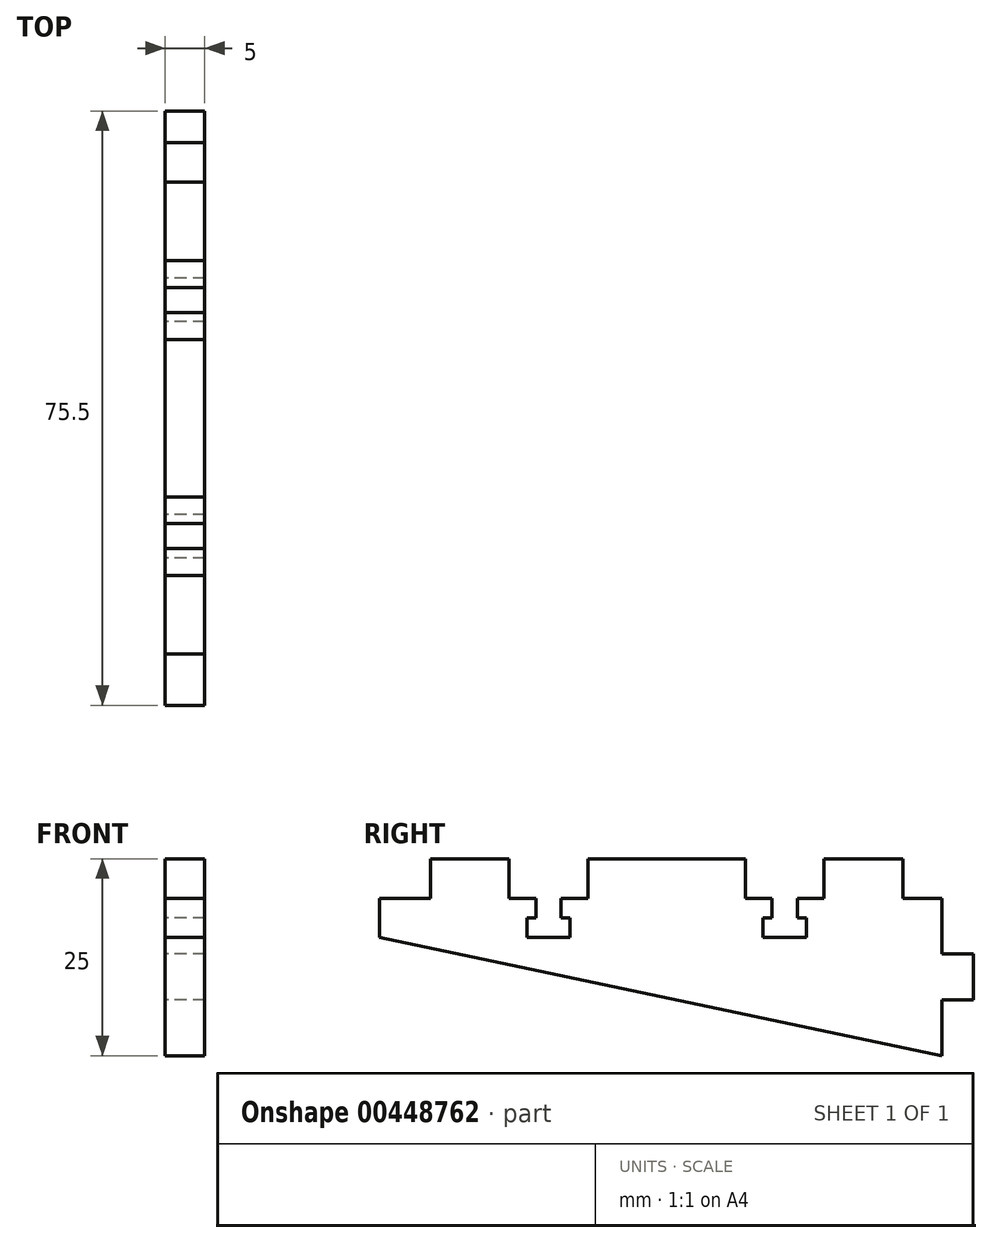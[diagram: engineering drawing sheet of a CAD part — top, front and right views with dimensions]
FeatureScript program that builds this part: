
annotation { "Feature Type Name" : "Feature", "Feature Type Description" : "" }
export const myFeature = defineFeature(function(context is Context, id is Id, definition is map)
    precondition{}
    {
        {
            assignVariable(context, id + "F0", {"name" : "thickness", "anyValue" : 5 * mm});
        }
        {
            var Q0;
            Q0=qCreatedBy(makeId("Right.planeOp"),FACE);
            var sketch = newSketch(context, id + "F1", { "sketchPlane" : qUnion([Q0])});
            skLineSegment(sketch, "E0", {"start": v(0, 0) * mm, "end": v(0, 7.1) * mm});
            skLineSegment(sketch, "E1", {"start": v(0, 20) * mm, "end": v(-5, 20) * mm});
            skLineSegment(sketch, "E2", {"start": v(-5, 20) * mm, "end": v(-5, 25) * mm});
            skLineSegment(sketch, "E3", {"start": v(-5, 25) * mm, "end": v(-15, 25) * mm});
            skLineSegment(sketch, "E4", {"start": v(-15, 25) * mm, "end": v(-15, 20) * mm});
            skLineSegment(sketch, "E5", {"start": v(-25, 20) * mm, "end": v(-25, 25) * mm});
            skLineSegment(sketch, "E6", {"start": v(-25, 25) * mm, "end": v(-45, 25) * mm});
            skLineSegment(sketch, "E7", {"start": v(-45, 25) * mm, "end": v(-45, 20) * mm});
            skLineSegment(sketch, "E8", {"start": v(-55, 20) * mm, "end": v(-55, 25) * mm});
            skLineSegment(sketch, "E9", {"start": v(-55, 25) * mm, "end": v(-65, 25) * mm});
            skLineSegment(sketch, "E10", {"start": v(-65, 25) * mm, "end": v(-65, 20) * mm});
            skLineSegment(sketch, "E11.trimOffspring", {"start": v(-65, 20) * mm, "end": v(-71.5, 20) * mm});
            skLineSegment(sketch, "E12.trimOffspring", {"start": v(-45, 20) * mm, "end": v(-48.4, 20) * mm});
            skLineSegment(sketch, "E13.trimOffspring", {"start": v(-15, 20) * mm, "end": v(-18.4, 20) * mm});
            skLineSegment(sketch, "E14", {"start": v(-20, 20) * mm, "end": v(-20, 4.2) * mm, "construction": true});
            skLineSegment(sketch, "E15", {"start": v(-35, 25) * mm, "end": v(-35, 7.34) * mm, "construction": true});
            skLineSegment(sketch, "E16", {"start": v(-21.6, 20) * mm, "end": v(-21.6, 17.5) * mm});
            skLineSegment(sketch, "E17", {"start": v(-21.6, 17.5) * mm, "end": v(-22.75, 17.5) * mm});
            skLineSegment(sketch, "E18", {"start": v(-22.75, 17.5) * mm, "end": v(-22.75, 15) * mm});
            skLineSegment(sketch, "E19", {"start": v(-22.75, 15) * mm, "end": v(-20, 15) * mm});
            skLineSegment(sketch, "E20.MirrorCS", {"start": v(-17.25, 15) * mm, "end": v(-20, 15) * mm});
            skLineSegment(sketch, "E21.MirrorCS", {"start": v(-17.25, 17.5) * mm, "end": v(-17.25, 15) * mm});
            skLineSegment(sketch, "E22.MirrorCS", {"start": v(-18.4, 17.5) * mm, "end": v(-17.25, 17.5) * mm});
            skLineSegment(sketch, "E23.MirrorCS", {"start": v(-18.4, 20) * mm, "end": v(-18.4, 17.5) * mm});
            skLineSegment(sketch, "E24.MirrorCS", {"start": v(-48.4, 20) * mm, "end": v(-48.4, 17.5) * mm});
            skLineSegment(sketch, "E25.MirrorCS", {"start": v(-48.4, 17.5) * mm, "end": v(-47.25, 17.5) * mm});
            skLineSegment(sketch, "E26.MirrorCS", {"start": v(-47.25, 17.5) * mm, "end": v(-47.25, 15) * mm});
            skLineSegment(sketch, "E27.MirrorCS", {"start": v(-47.25, 15) * mm, "end": v(-50, 15) * mm});
            skLineSegment(sketch, "E28.MirrorCS", {"start": v(-52.75, 15) * mm, "end": v(-50, 15) * mm});
            skLineSegment(sketch, "E29.MirrorCS", {"start": v(-52.75, 17.5) * mm, "end": v(-52.75, 15) * mm});
            skLineSegment(sketch, "E30.MirrorCS", {"start": v(-51.6, 20) * mm, "end": v(-51.6, 17.5) * mm});
            skLineSegment(sketch, "E31.MirrorCS", {"start": v(-51.6, 17.5) * mm, "end": v(-52.75, 17.5) * mm});
            skLineSegment(sketch, "E32.trimOffspring", {"start": v(-51.6, 20) * mm, "end": v(-55, 20) * mm});
            skLineSegment(sketch, "E33.trimOffspring", {"start": v(-21.6, 20) * mm, "end": v(-25, 20) * mm});
            skLineSegment(sketch, "E34", {"start": v(-71.5, 20) * mm, "end": v(-71.5, 15) * mm});
            skLineSegment(sketch, "E35", {"start": v(-71.5, 15) * mm, "end": v(0, 0) * mm});
            skLineSegment(sketch, "E36", {"start": v(0, 12.9) * mm, "end": v(4, 12.9) * mm});
            skLineSegment(sketch, "E37", {"start": v(4, 12.9) * mm, "end": v(4, 7.1) * mm});
            skLineSegment(sketch, "E38", {"start": v(4, 7.1) * mm, "end": v(0, 7.1) * mm});
            skPoint(sketch, "E39", {"position": v(4, 10) * mm});
            skPoint(sketch, "E40", {"position": v(0, 10) * mm});
            skLineSegment(sketch, "E41.trimOffspring", {"start": v(0, 12.9) * mm, "end": v(0, 20) * mm});
            skSolve(sketch);
        }
        {
            var Q0;
            Q0=qSketchRegion(id+"F1",true);
            extrude(context, id + "F2", {"entities" : qUnion([Q0]), "depth" : getVariable(context, 'thickness')});
        }
    });
